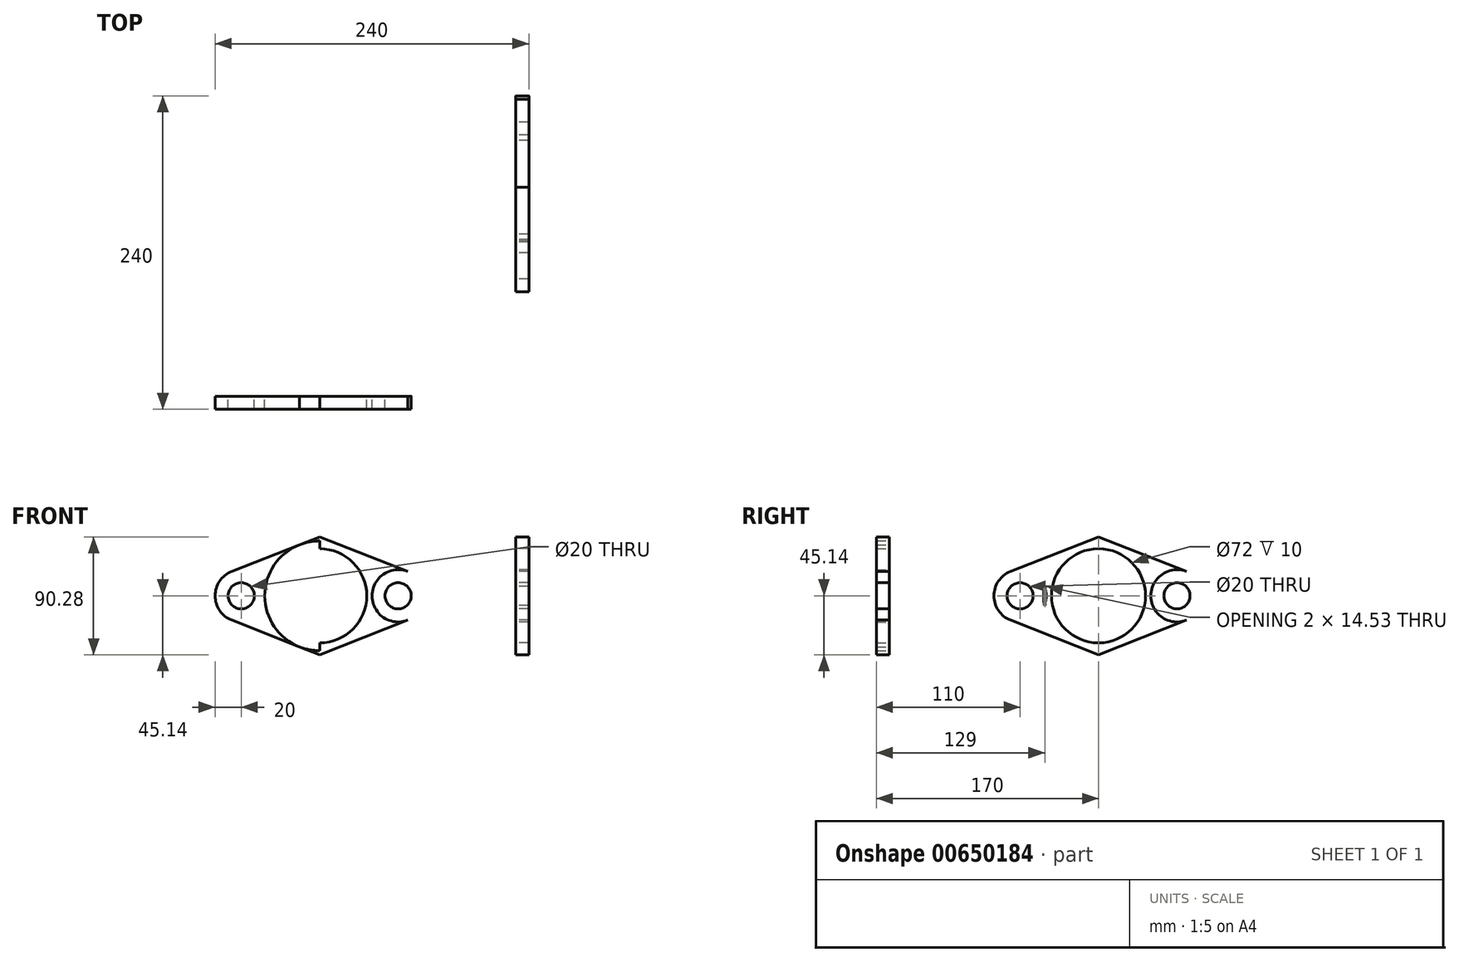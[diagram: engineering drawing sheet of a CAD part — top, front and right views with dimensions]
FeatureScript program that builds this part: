
annotation { "Feature Type Name" : "Feature", "Feature Type Description" : "" }
export const myFeature = defineFeature(function(context is Context, id is Id, definition is map)
    precondition{}
    {
        {
            var Q0;
            Q0=qCreatedBy(makeId("Right.planeOp"),FACE);
            var sketch = newSketch(context, id + "F0", { "sketchPlane" : qUnion([Q0])});
            skCircle(sketch, "E0", {"center": v(0, 0) * mm, "radius": 36 * mm});
            skCircle(sketch, "E1", {"center": v(0, 0) * mm, "radius": 30 * mm});
            skCircle(sketch, "E2", {"center": v(0, 0) * mm, "radius": 42 * mm});
            skCircle(sketch, "E3", {"center": v(-60, 0) * mm, "radius": 10 * mm});
            skCircle(sketch, "E4", {"center": v(-60, 0) * mm, "radius": 20 * mm});
            skCircle(sketch, "E5.MirrorC", {"center": v(60, 0) * mm, "radius": 20 * mm});
            skCircle(sketch, "E6.MirrorC", {"center": v(60, 0) * mm, "radius": 10 * mm});
            skLineSegment(sketch, "E7", {"start": v(-104.39, 4) * mm, "end": v(35.9, 59.3) * mm});
            skLineSegment(sketch, "E8", {"start": v(-111.23, -1.3) * mm, "end": v(61.52, -69.4) * mm});
            skLineSegment(sketch, "E9", {"start": v(158.05, 17.15) * mm, "end": v(-15.29, -51.17) * mm});
            skLineSegment(sketch, "E10", {"start": v(-32.76, 58.05) * mm, "end": v(175.7, -24.1) * mm});
            skSolve(sketch);
        }
        {
            var Q0;
            Q0=qCreatedBy(makeId("Top.planeOp"),FACE);
            var sketch = newSketch(context, id + "F1", { "sketchPlane" : qUnion([Q0])});
            skLineSegment(sketch, "E11", {"start": v(0, 0) * mm, "end": v(-90, 0) * mm});
            skLineSegment(sketch, "E12", {"start": v(-150, -60) * mm, "end": v(-150, -160) * mm});
            skPoint(sketch, "E13.visualSharp", {"position": v(-150, 0) * mm});
            skArc(sketch, "E13.filletArc", {"start": v(-90, 0) * mm, "mid": v(-132.43, -17.57) * mm, "end": v(-150, -60) * mm});
            skSolve(sketch);
        }
        {
            var Q0;
            Q0=qCreatedBy(makeId("Front.planeOp"),FACE);
            cPlane(context, id + "F2", {"entities" : qUnion([Q0]), "cplaneType" : CPlaneType.OFFSET, "offset" : 160 * mm, "width" : 150 * mm, "height" : 150 * mm});
        }
        {
            var Q0;
            Q0=qCreatedBy(id+"F2.planeOp",FACE);
            var sketch = newSketch(context, id + "F3", { "sketchPlane" : qUnion([Q0])});
            skPoint(sketch, "E14.0", {"position": v(-150, 0) * mm});
            skCircle(sketch, "E15", {"center": v(-150, 0) * mm, "radius": 36 * mm});
            skCircle(sketch, "E16", {"center": v(-150, 0) * mm, "radius": 42 * mm});
            skPoint(sketch, "E17.0", {"position": v(-185.73, 10.29) * mm});
            skCircle(sketch, "E18", {"center": v(-210, 0) * mm, "radius": 10 * mm});
            skCircle(sketch, "E19", {"center": v(-210, 0) * mm, "radius": 20 * mm});
            skLineSegment(sketch, "E20", {"start": v(-150, -53.07) * mm, "end": v(-150, 65) * mm});
            skCircle(sketch, "E21.MirrorC", {"center": v(-90, 0) * mm, "radius": 20 * mm});
            skCircle(sketch, "E22.MirrorC", {"center": v(-90, 0) * mm, "radius": 10 * mm});
            skLineSegment(sketch, "E23", {"start": v(-217.33, 18.6) * mm, "end": v(-87.96, 69.6) * mm});
            skLineSegment(sketch, "E24", {"start": v(-82.67, 18.6) * mm, "end": v(-234.38, 78.4) * mm});
            skLineSegment(sketch, "E25", {"start": v(-275.21, 4.2) * mm, "end": v(-264.55, 0) * mm});
            skLineSegment(sketch, "E26", {"start": v(-82.67, -18.6) * mm, "end": v(-247.43, -83.54) * mm});
            skPoint(sketch, "E27.orphan", {"position": v(-264.55, 0) * mm});
            skLineSegment(sketch, "E28.trimOffspring", {"start": v(-217.33, -18.6) * mm, "end": v(-94.02, -67.2) * mm});
            skPoint(sketch, "E29.orphan", {"position": v(-35.45, 0) * mm});
            skSolve(sketch);
        }
        {
            var Q0;
            {var subQ0=sQuery(id+"F3.wireOp",EDGE,"E23");var subQ1=sQuery(id+"F3.wireOp",EDGE,"E16");var subQ2=makeQuery(id+"F3.imprint","INTERSECT",VERTEX,{"derivedFrom":[subQ1,subQ0]});Q0=makeQuery(id+"F3.imprint","IMPRINT",FACE,{"disambiguationData":[TD([[makeQuery(id+"F3.imprint","IMPRINT",EDGE,{"disambiguationData":[TD([[subQ2,-1.0]])],"derivedFrom":subQ1}),-1.0]])]});}
            var Q1;
            {var subQ0=sQuery(id+"F3.wireOp",EDGE,"E24");var subQ1=sQuery(id+"F3.wireOp",EDGE,"E16");var subQ2=makeQuery(id+"F3.imprint","INTERSECT",VERTEX,{"derivedFrom":[subQ1,subQ0]});Q1=makeQuery(id+"F3.imprint","IMPRINT",FACE,{"disambiguationData":[TD([[makeQuery(id+"F3.imprint","IMPRINT",EDGE,{"disambiguationData":[TD([[subQ2,1.0]])],"derivedFrom":subQ1}),-1.0]])]});}
            var Q2;
            {var subQ0=sQuery(id+"F3.wireOp",EDGE,"E26");var subQ1=sQuery(id+"F3.wireOp",EDGE,"E16");var subQ2=makeQuery(id+"F3.imprint","INTERSECT",VERTEX,{"derivedFrom":[subQ1,subQ0]});Q2=makeQuery(id+"F3.imprint","IMPRINT",FACE,{"disambiguationData":[TD([[makeQuery(id+"F3.imprint","IMPRINT",EDGE,{"disambiguationData":[TD([[subQ2,-1.0]])],"derivedFrom":subQ1}),-1.0]])]});}
            var Q3;
            {var subQ0=sQuery(id+"F3.wireOp",EDGE,"E28.trimOffspring");var subQ1=sQuery(id+"F3.wireOp",EDGE,"E16");var subQ2=makeQuery(id+"F3.imprint","INTERSECT",VERTEX,{"derivedFrom":[subQ1,subQ0]});Q3=makeQuery(id+"F3.imprint","IMPRINT",FACE,{"disambiguationData":[TD([[makeQuery(id+"F3.imprint","IMPRINT",EDGE,{"disambiguationData":[TD([[subQ2,1.0]])],"derivedFrom":subQ1}),-1.0]])]});}
            var Q4;
            Q4=makeQuery(id+"F3.imprint","IMPRINT",FACE,{"disambiguationData":[TD([[makeQuery(id+"F3.imprint","IMPRINT",EDGE,{"derivedFrom":sQuery(id+"F3.wireOp",EDGE,"E18")}),-1.0]])]});
            var Q5;
            Q5=makeQuery(id+"F3.imprint","IMPRINT",FACE,{"disambiguationData":[TD([[makeQuery(id+"F3.imprint","IMPRINT",EDGE,{"derivedFrom":sQuery(id+"F3.wireOp",EDGE,"E22.MirrorC")}),1.0]])]});
            var Q6;
            {var subQ0=sQuery(id+"F3.wireOp",EDGE,"E21.MirrorC");var subQ1=sQuery(id+"F3.wireOp",EDGE,"E16");var subQ2=makeQuery(id+"F3.imprint","INTERSECT",VERTEX,{"disambiguationData":[OD(0.0)],"derivedFrom":[subQ1,subQ0]});Q6=makeQuery(id+"F3.imprint","IMPRINT",FACE,{"disambiguationData":[TD([[makeQuery(id+"F3.imprint","IMPRINT",EDGE,{"disambiguationData":[TD([[subQ2,1.0]])],"derivedFrom":subQ1}),1.0]])]});}
            var Q7;
            {var subQ0=sQuery(id+"F3.wireOp",EDGE,"E23");var subQ1=sQuery(id+"F3.wireOp",EDGE,"E16");var subQ2=makeQuery(id+"F3.imprint","INTERSECT",VERTEX,{"derivedFrom":[subQ1,subQ0]});Q7=makeQuery(id+"F3.imprint","IMPRINT",FACE,{"disambiguationData":[TD([[makeQuery(id+"F3.imprint","IMPRINT",EDGE,{"disambiguationData":[TD([[subQ2,1.0]])],"derivedFrom":subQ1}),-1.0]])]});}
            var Q8;
            {var subQ0=sQuery(id+"F3.wireOp",EDGE,"E24");var subQ1=sQuery(id+"F3.wireOp",EDGE,"E16");var subQ2=makeQuery(id+"F3.imprint","INTERSECT",VERTEX,{"derivedFrom":[subQ1,subQ0]});Q8=makeQuery(id+"F3.imprint","IMPRINT",FACE,{"disambiguationData":[TD([[makeQuery(id+"F3.imprint","IMPRINT",EDGE,{"disambiguationData":[TD([[subQ2,-1.0]])],"derivedFrom":subQ1}),-1.0]])]});}
            var Q9;
            {var subQ0=sQuery(id+"F3.wireOp",EDGE,"E28.trimOffspring");var subQ1=sQuery(id+"F3.wireOp",EDGE,"E16");var subQ2=makeQuery(id+"F3.imprint","INTERSECT",VERTEX,{"derivedFrom":[subQ1,subQ0]});Q9=makeQuery(id+"F3.imprint","IMPRINT",FACE,{"disambiguationData":[TD([[makeQuery(id+"F3.imprint","IMPRINT",EDGE,{"disambiguationData":[TD([[subQ2,-1.0]])],"derivedFrom":subQ1}),-1.0]])]});}
            var Q10;
            {var subQ0=sQuery(id+"F3.wireOp",EDGE,"E26");var subQ1=sQuery(id+"F3.wireOp",EDGE,"E16");var subQ2=makeQuery(id+"F3.imprint","INTERSECT",VERTEX,{"derivedFrom":[subQ1,subQ0]});Q10=makeQuery(id+"F3.imprint","IMPRINT",FACE,{"disambiguationData":[TD([[makeQuery(id+"F3.imprint","IMPRINT",EDGE,{"disambiguationData":[TD([[subQ2,1.0]])],"derivedFrom":subQ1}),-1.0]])]});}
            extrude(context, id + "F4", {"entities" : qUnion([Q0, Q1, Q2, Q3, Q4, Q5, Q6, Q7, Q8, Q9, Q10]), "depth" : 10 * mm, "offsetDistance" : 25 * mm});
        }
        {
            var Q0;
            {var subQ0=sQuery(id+"F0.wireOp",EDGE,"E10");var subQ1=sQuery(id+"F0.wireOp",EDGE,"E2");var subQ2=makeQuery(id+"F0.imprint","INTERSECT",VERTEX,{"derivedFrom":[subQ1,subQ0]});Q0=makeQuery(id+"F0.imprint","IMPRINT",FACE,{"disambiguationData":[TD([[makeQuery(id+"F0.imprint","IMPRINT",EDGE,{"disambiguationData":[TD([[subQ2,-1.0]])],"derivedFrom":subQ1}),-1.0]])]});}
            var Q1;
            {var subQ0=sQuery(id+"F0.wireOp",EDGE,"E7");var subQ1=sQuery(id+"F0.wireOp",EDGE,"E2");var subQ2=makeQuery(id+"F0.imprint","INTERSECT",VERTEX,{"derivedFrom":[subQ1,subQ0]});Q1=makeQuery(id+"F0.imprint","IMPRINT",FACE,{"disambiguationData":[TD([[makeQuery(id+"F0.imprint","IMPRINT",EDGE,{"disambiguationData":[TD([[subQ2,-1.0]])],"derivedFrom":subQ1}),-1.0]])]});}
            var Q2;
            {var subQ0=sQuery(id+"F0.wireOp",EDGE,"E8");var subQ1=sQuery(id+"F0.wireOp",EDGE,"E2");var subQ2=makeQuery(id+"F0.imprint","INTERSECT",VERTEX,{"derivedFrom":[subQ1,subQ0]});Q2=makeQuery(id+"F0.imprint","IMPRINT",FACE,{"disambiguationData":[TD([[makeQuery(id+"F0.imprint","IMPRINT",EDGE,{"disambiguationData":[TD([[subQ2,1.0]])],"derivedFrom":subQ1}),-1.0]])]});}
            var Q3;
            Q3=makeQuery(id+"F0.imprint","IMPRINT",FACE,{"disambiguationData":[TD([[makeQuery(id+"F0.imprint","IMPRINT",EDGE,{"derivedFrom":sQuery(id+"F0.wireOp",EDGE,"E3")}),-1.0]])]});
            var Q4;
            {var subQ0=sQuery(id+"F0.wireOp",EDGE,"E10");var subQ1=sQuery(id+"F0.wireOp",EDGE,"E2");var subQ2=makeQuery(id+"F0.imprint","INTERSECT",VERTEX,{"derivedFrom":[subQ1,subQ0]});Q4=makeQuery(id+"F0.imprint","IMPRINT",FACE,{"disambiguationData":[TD([[makeQuery(id+"F0.imprint","IMPRINT",EDGE,{"disambiguationData":[TD([[subQ2,1.0]])],"derivedFrom":subQ1}),-1.0]])]});}
            var Q5;
            Q5=makeQuery(id+"F0.imprint","IMPRINT",FACE,{"disambiguationData":[TD([[makeQuery(id+"F0.imprint","IMPRINT",EDGE,{"derivedFrom":sQuery(id+"F0.wireOp",EDGE,"E6.MirrorC")}),1.0]])]});
            var Q6;
            {var subQ0=sQuery(id+"F0.wireOp",EDGE,"E5.MirrorC");var subQ1=sQuery(id+"F0.wireOp",EDGE,"E2");var subQ2=makeQuery(id+"F0.imprint","INTERSECT",VERTEX,{"disambiguationData":[OD(0.0)],"derivedFrom":[subQ1,subQ0]});Q6=makeQuery(id+"F0.imprint","IMPRINT",FACE,{"disambiguationData":[TD([[makeQuery(id+"F0.imprint","IMPRINT",EDGE,{"disambiguationData":[TD([[subQ2,1.0]])],"derivedFrom":subQ1}),1.0]])]});}
            var Q7;
            {var subQ0=sQuery(id+"F0.wireOp",EDGE,"E9");var subQ1=sQuery(id+"F0.wireOp",EDGE,"E2");var subQ2=makeQuery(id+"F0.imprint","INTERSECT",VERTEX,{"derivedFrom":[subQ1,subQ0]});Q7=makeQuery(id+"F0.imprint","IMPRINT",FACE,{"disambiguationData":[TD([[makeQuery(id+"F0.imprint","IMPRINT",EDGE,{"disambiguationData":[TD([[subQ2,-1.0]])],"derivedFrom":subQ1}),-1.0]])]});}
            var Q8;
            {var subQ0=sQuery(id+"F0.wireOp",EDGE,"E8");var subQ1=sQuery(id+"F0.wireOp",EDGE,"E2");var subQ2=makeQuery(id+"F0.imprint","INTERSECT",VERTEX,{"derivedFrom":[subQ1,subQ0]});Q8=makeQuery(id+"F0.imprint","IMPRINT",FACE,{"disambiguationData":[TD([[makeQuery(id+"F0.imprint","IMPRINT",EDGE,{"disambiguationData":[TD([[subQ2,-1.0]])],"derivedFrom":subQ1}),-1.0]])]});}
            extrude(context, id + "F5", {"entities" : qUnion([Q0, Q1, Q2, Q3, Q4, Q5, Q6, Q7, Q8]), "flatOperationType" : FlatOperationType.REMOVE, "depth" : 10 * mm, "offsetDistance" : 25 * mm, "domain" : OperationDomain.MODEL});
        }
    });
